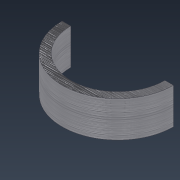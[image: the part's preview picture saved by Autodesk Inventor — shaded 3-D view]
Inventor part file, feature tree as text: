
AUTODESK INVENTOR PART (.ipt)
format: ipt  version: 2022 (Build 260153000, 153)  size: 102,400 bytes
history: native  units: mm
features: extrude x1, sketch x1
ambient origin geometry x8: Origin, YZ Plane, XZ Plane, XY Plane, X Axis, Y Axis, Z Axis, Center Point
bodies: Solid1 (feature_tree)
feature tree (2):
  extrude  "Extrusion1"  Depth=21.0mm
  sketch  "Sketch1"  dims[d0=55.0mm d1=65.0mm d2=21.0mm d3=0.0mm]
